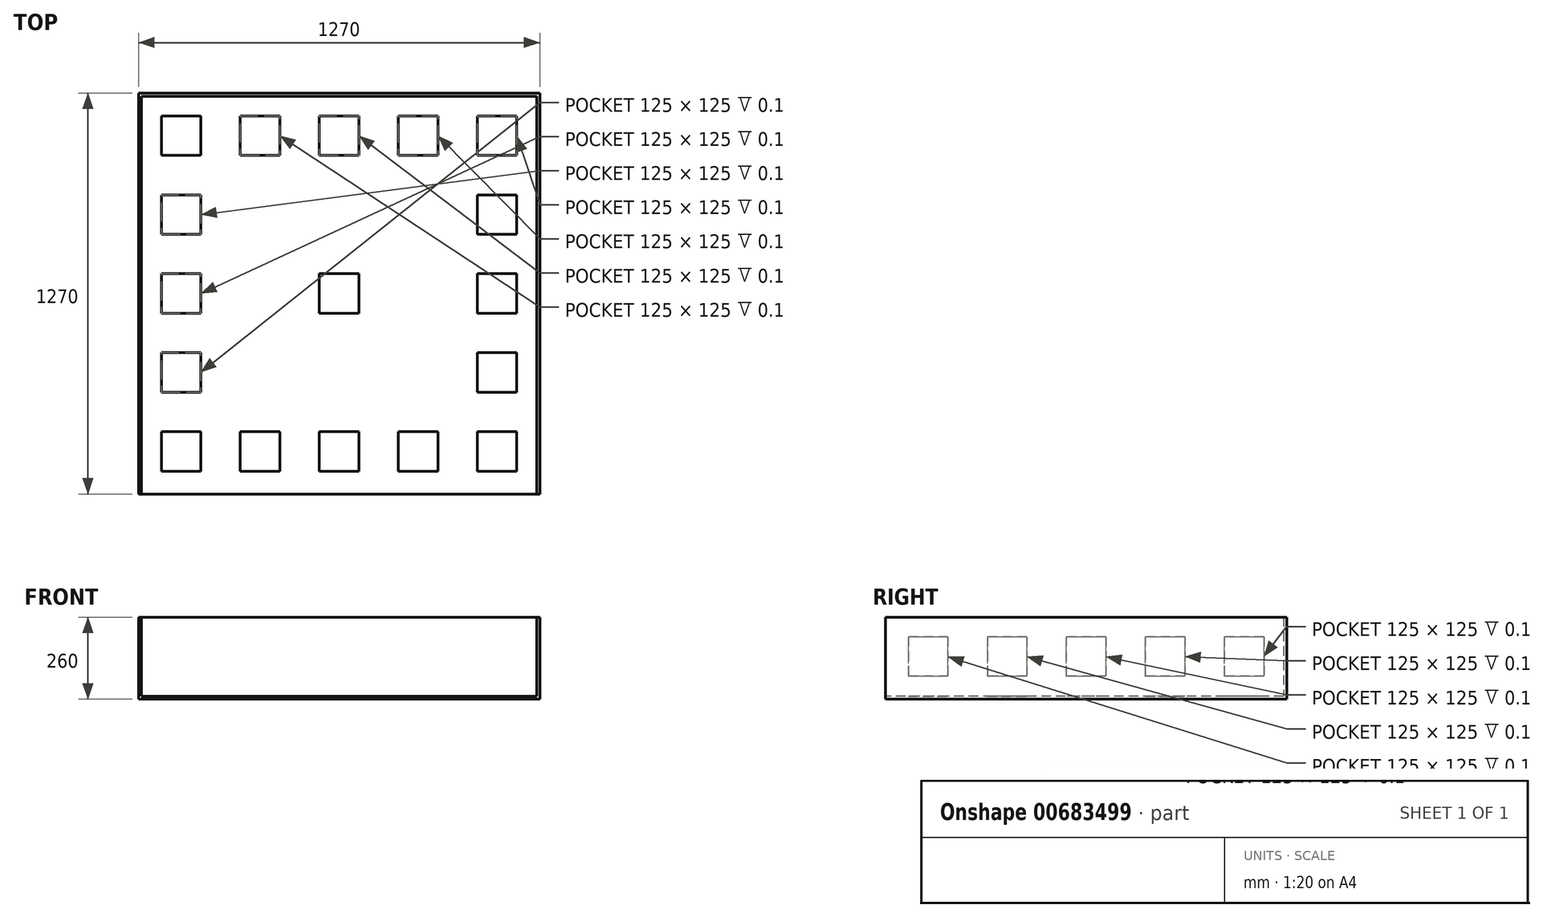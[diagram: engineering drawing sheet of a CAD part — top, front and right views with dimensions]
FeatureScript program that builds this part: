
annotation { "Feature Type Name" : "Feature", "Feature Type Description" : "" }
export const myFeature = defineFeature(function(context is Context, id is Id, definition is map)
    precondition{}
    {
        {
            var Q0;
            Q0=qCreatedBy(makeId("Top.planeOp"),FACE);
            var sketch = newSketch(context, id + "F0", { "sketchPlane" : qUnion([Q0])});
            skLineSegment(sketch, "E0.bottom", {"start": v(500, 500) * mm, "end": v(-500, 500) * mm, "construction": true});
            skLineSegment(sketch, "E0.top", {"start": v(500, -500) * mm, "end": v(-500, -500) * mm, "construction": true});
            skLineSegment(sketch, "E0.left", {"start": v(500, 500) * mm, "end": v(500, -500) * mm, "construction": true});
            skLineSegment(sketch, "E0.right", {"start": v(-500, 500) * mm, "end": v(-500, -500) * mm, "construction": true});
            skPoint(sketch, "E0.middle", {"position": v(0, 0) * mm});
            skLineSegment(sketch, "E1.bottom", {"start": v(-562.5, 562.5) * mm, "end": v(-437.5, 562.5) * mm});
            skLineSegment(sketch, "E1.top", {"start": v(-562.5, 437.5) * mm, "end": v(-437.5, 437.5) * mm});
            skLineSegment(sketch, "E1.left", {"start": v(-562.5, 562.5) * mm, "end": v(-562.5, 437.5) * mm});
            skLineSegment(sketch, "E1.right", {"start": v(-437.5, 562.5) * mm, "end": v(-437.5, 437.5) * mm});
            skPoint(sketch, "E1.middle", {"position": v(-500, 500) * mm});
            skLineSegment(sketch, "E2.1.0.0", {"start": v(-312.5, 562.5) * mm, "end": v(-187.5, 562.5) * mm});
            skLineSegment(sketch, "E2.1.0.1", {"start": v(-187.5, 562.5) * mm, "end": v(-187.5, 437.5) * mm});
            skLineSegment(sketch, "E2.1.0.2", {"start": v(-312.5, 437.5) * mm, "end": v(-187.5, 437.5) * mm});
            skLineSegment(sketch, "E2.1.0.3", {"start": v(-312.5, 562.5) * mm, "end": v(-312.5, 437.5) * mm});
            skLineSegment(sketch, "E2.2.0.0", {"start": v(-62.5, 562.5) * mm, "end": v(62.5, 562.5) * mm});
            skLineSegment(sketch, "E2.2.0.1", {"start": v(62.5, 562.5) * mm, "end": v(62.5, 437.5) * mm});
            skLineSegment(sketch, "E2.2.0.2", {"start": v(-62.5, 437.5) * mm, "end": v(62.5, 437.5) * mm});
            skLineSegment(sketch, "E2.2.0.3", {"start": v(-62.5, 562.5) * mm, "end": v(-62.5, 437.5) * mm});
            skLineSegment(sketch, "E2.3.0.0", {"start": v(187.5, 562.5) * mm, "end": v(312.5, 562.5) * mm});
            skLineSegment(sketch, "E2.3.0.1", {"start": v(312.5, 562.5) * mm, "end": v(312.5, 437.5) * mm});
            skLineSegment(sketch, "E2.3.0.2", {"start": v(187.5, 437.5) * mm, "end": v(312.5, 437.5) * mm});
            skLineSegment(sketch, "E2.3.0.3", {"start": v(187.5, 562.5) * mm, "end": v(187.5, 437.5) * mm});
            skLineSegment(sketch, "E2.4.0.0", {"start": v(437.5, 562.5) * mm, "end": v(562.5, 562.5) * mm});
            skLineSegment(sketch, "E2.4.0.1", {"start": v(562.5, 562.5) * mm, "end": v(562.5, 437.5) * mm});
            skLineSegment(sketch, "E2.4.0.2", {"start": v(437.5, 437.5) * mm, "end": v(562.5, 437.5) * mm});
            skLineSegment(sketch, "E2.4.0.3", {"start": v(437.5, 562.5) * mm, "end": v(437.5, 437.5) * mm});
            skLineSegment(sketch, "E2.direction1", {"start": v(-562.5, 562.5) * mm, "end": v(-312.5, 562.5) * mm, "construction": true});
            skLineSegment(sketch, "E3.0.1.0", {"start": v(-437.5, 312.5) * mm, "end": v(-437.5, 187.5) * mm});
            skLineSegment(sketch, "E3.0.1.1", {"start": v(-562.5, 312.5) * mm, "end": v(-562.5, 187.5) * mm});
            skLineSegment(sketch, "E3.0.1.2", {"start": v(-562.5, 187.5) * mm, "end": v(-437.5, 187.5) * mm});
            skLineSegment(sketch, "E3.0.2.0", {"start": v(-437.5, 62.5) * mm, "end": v(-437.5, -62.5) * mm});
            skLineSegment(sketch, "E3.0.2.1", {"start": v(-562.5, 62.5) * mm, "end": v(-562.5, -62.5) * mm});
            skLineSegment(sketch, "E3.0.2.2", {"start": v(-562.5, -62.5) * mm, "end": v(-437.5, -62.5) * mm});
            skLineSegment(sketch, "E3.0.3.0", {"start": v(-437.5, -187.5) * mm, "end": v(-437.5, -312.5) * mm});
            skLineSegment(sketch, "E3.0.3.1", {"start": v(-562.5, -187.5) * mm, "end": v(-562.5, -312.5) * mm});
            skLineSegment(sketch, "E3.0.3.2", {"start": v(-562.5, -312.5) * mm, "end": v(-437.5, -312.5) * mm});
            skLineSegment(sketch, "E3.0.4.0", {"start": v(-437.5, -437.5) * mm, "end": v(-437.5, -562.5) * mm});
            skLineSegment(sketch, "E3.0.4.1", {"start": v(-562.5, -437.5) * mm, "end": v(-562.5, -562.5) * mm});
            skLineSegment(sketch, "E3.0.4.2", {"start": v(-562.5, -562.5) * mm, "end": v(-437.5, -562.5) * mm});
            skLineSegment(sketch, "E3.direction1", {"start": v(-437.5, 437.5) * mm, "end": v(-412.1, 437.5) * mm, "construction": true});
            skLineSegment(sketch, "E3.direction2", {"start": v(-437.5, 437.5) * mm, "end": v(-437.5, 187.5) * mm, "construction": true});
            skLineSegment(sketch, "E4", {"start": v(-562.5, 312.5) * mm, "end": v(-437.5, 312.5) * mm});
            skLineSegment(sketch, "E5", {"start": v(-562.5, 62.5) * mm, "end": v(-437.5, 62.5) * mm});
            skLineSegment(sketch, "E6", {"start": v(-562.5, -187.5) * mm, "end": v(-437.5, -187.5) * mm});
            skLineSegment(sketch, "E7", {"start": v(-562.5, -437.5) * mm, "end": v(-437.5, -437.5) * mm});
            skLineSegment(sketch, "E8", {"start": v(500, 500) * mm, "end": v(-500, -500) * mm, "construction": true});
            skLineSegment(sketch, "E9.MirrorCS", {"start": v(437.5, -437.5) * mm, "end": v(437.5, -412.1) * mm, "construction": true});
            skLineSegment(sketch, "E10.MirrorCS", {"start": v(312.5, -437.5) * mm, "end": v(187.5, -437.5) * mm});
            skLineSegment(sketch, "E11.MirrorCS", {"start": v(562.5, -562.5) * mm, "end": v(562.5, -437.5) * mm});
            skPoint(sketch, "E12.MirrorP", {"position": v(500, -500) * mm});
            skLineSegment(sketch, "E13.MirrorCS", {"start": v(437.5, 187.5) * mm, "end": v(437.5, 312.5) * mm});
            skLineSegment(sketch, "E14.MirrorCS", {"start": v(312.5, -562.5) * mm, "end": v(187.5, -562.5) * mm});
            skLineSegment(sketch, "E15.MirrorCS", {"start": v(-187.5, -437.5) * mm, "end": v(-312.5, -437.5) * mm});
            skLineSegment(sketch, "E16.MirrorCS", {"start": v(562.5, -562.5) * mm, "end": v(562.5, -312.5) * mm, "construction": true});
            skLineSegment(sketch, "E17.MirrorCS", {"start": v(437.5, -437.5) * mm, "end": v(187.5, -437.5) * mm, "construction": true});
            skLineSegment(sketch, "E18.MirrorCS", {"start": v(562.5, 187.5) * mm, "end": v(437.5, 187.5) * mm});
            skLineSegment(sketch, "E19.MirrorCS", {"start": v(562.5, 62.5) * mm, "end": v(437.5, 62.5) * mm});
            skLineSegment(sketch, "E20.MirrorCS", {"start": v(437.5, -62.5) * mm, "end": v(437.5, 62.5) * mm});
            skLineSegment(sketch, "E21.MirrorCS", {"start": v(562.5, -62.5) * mm, "end": v(437.5, -62.5) * mm});
            skLineSegment(sketch, "E22.MirrorCS", {"start": v(437.5, -562.5) * mm, "end": v(437.5, -437.5) * mm});
            skLineSegment(sketch, "E23.MirrorCS", {"start": v(562.5, -562.5) * mm, "end": v(437.5, -562.5) * mm});
            skLineSegment(sketch, "E24.MirrorCS", {"start": v(562.5, 187.5) * mm, "end": v(562.5, 312.5) * mm});
            skLineSegment(sketch, "E25.MirrorCS", {"start": v(62.5, -562.5) * mm, "end": v(-62.5, -562.5) * mm});
            skLineSegment(sketch, "E26.MirrorCS", {"start": v(-187.5, -562.5) * mm, "end": v(-187.5, -437.5) * mm});
            skLineSegment(sketch, "E27.MirrorCS", {"start": v(312.5, -562.5) * mm, "end": v(312.5, -437.5) * mm});
            skLineSegment(sketch, "E28.MirrorCS", {"start": v(187.5, -562.5) * mm, "end": v(187.5, -437.5) * mm});
            skLineSegment(sketch, "E29.MirrorCS", {"start": v(562.5, -312.5) * mm, "end": v(437.5, -312.5) * mm});
            skLineSegment(sketch, "E30.MirrorCS", {"start": v(437.5, -312.5) * mm, "end": v(437.5, -187.5) * mm});
            skLineSegment(sketch, "E31.MirrorCS", {"start": v(562.5, -187.5) * mm, "end": v(437.5, -187.5) * mm});
            skLineSegment(sketch, "E32.MirrorCS", {"start": v(-312.5, -562.5) * mm, "end": v(-312.5, -437.5) * mm});
            skLineSegment(sketch, "E33.MirrorCS", {"start": v(562.5, 312.5) * mm, "end": v(437.5, 312.5) * mm});
            skLineSegment(sketch, "E34.MirrorCS", {"start": v(562.5, -312.5) * mm, "end": v(562.5, -187.5) * mm});
            skLineSegment(sketch, "E35.MirrorCS", {"start": v(62.5, -437.5) * mm, "end": v(-62.5, -437.5) * mm});
            skLineSegment(sketch, "E36.MirrorCS", {"start": v(62.5, -562.5) * mm, "end": v(62.5, -437.5) * mm});
            skLineSegment(sketch, "E37.MirrorCS", {"start": v(562.5, -437.5) * mm, "end": v(437.5, -437.5) * mm});
            skLineSegment(sketch, "E38.MirrorCS", {"start": v(-62.5, -562.5) * mm, "end": v(-62.5, -437.5) * mm});
            skLineSegment(sketch, "E39.MirrorCS", {"start": v(562.5, -62.5) * mm, "end": v(562.5, 62.5) * mm});
            skLineSegment(sketch, "E40.MirrorCS", {"start": v(-187.5, -562.5) * mm, "end": v(-312.5, -562.5) * mm});
            skLineSegment(sketch, "E41.bottom", {"start": v(-62.5, 62.5) * mm, "end": v(62.5, 62.5) * mm});
            skLineSegment(sketch, "E41.top", {"start": v(-62.5, -62.5) * mm, "end": v(62.5, -62.5) * mm});
            skLineSegment(sketch, "E41.left", {"start": v(-62.5, 62.5) * mm, "end": v(-62.5, -62.5) * mm});
            skLineSegment(sketch, "E41.right", {"start": v(62.5, 62.5) * mm, "end": v(62.5, -62.5) * mm});
            skSolve(sketch);
        }
        {
            var Q0;
            Q0=qCreatedBy(makeId("Top.planeOp"),FACE);
            var sketch = newSketch(context, id + "F1", { "sketchPlane" : qUnion([Q0])});
            skLineSegment(sketch, "E42.bottom", {"start": v(-625, 625) * mm, "end": v(625, 625) * mm});
            skLineSegment(sketch, "E42.top", {"start": v(-625, -625) * mm, "end": v(625, -625) * mm});
            skLineSegment(sketch, "E42.left", {"start": v(-625, 625) * mm, "end": v(-625, -625) * mm});
            skLineSegment(sketch, "E42.right", {"start": v(625, 625) * mm, "end": v(625, -625) * mm});
            skPoint(sketch, "E42.middle", {"position": v(0, 0) * mm});
            skSolve(sketch);
        }
        {
            var Q0;
            Q0 = qSketchRegion(id + "F1", true);
            extrude(context, id + "F2", {"entities" : qUnion([Q0]), "oppositeDirection" : true, "depth" : 10 * mm, "offsetDistance" : 25.4 * mm});
        }
        {
            var Q0;
            Q0 = qSketchRegion(id + "F0", true);
            extrude(context, id + "F3", {"entities" : qUnion([Q0]), "operationType" : NewBodyOperationType.REMOVE, "oppositeDirection" : true, "depth" : 0.1 * mm, "offsetDistance" : 25.4 * mm});
        }
        {
            var Q0;
            Q0=makeQuery(id+"F2.opExtrude","CAP_FACE",FACE,{"disambiguationData":[OSD([sQuery(id+"F1.wireOp",EDGE,"E42.bottom"),sQuery(id+"F1.wireOp",EDGE,"E42.top"),sQuery(id+"F1.wireOp",EDGE,"E42.left"),sQuery(id+"F1.wireOp",EDGE,"E42.right")])],"isStart":false});
            var sketch = newSketch(context, id + "F4", { "sketchPlane" : qUnion([Q0])});
            skLineSegment(sketch, "E43.bottom", {"start": v(635, 635) * mm, "end": v(-635, 635) * mm});
            skLineSegment(sketch, "E43.top", {"start": v(635, -635) * mm, "end": v(-635, -635) * mm});
            skLineSegment(sketch, "E43.left", {"start": v(635, 635) * mm, "end": v(635, -635) * mm});
            skLineSegment(sketch, "E43.right", {"start": v(-635, 635) * mm, "end": v(-635, -635) * mm});
            skPoint(sketch, "E43.middle", {"position": v(0, 0) * mm});
            skLineSegment(sketch, "E44.bottom", {"start": v(-625, 625) * mm, "end": v(625, 625) * mm});
            skLineSegment(sketch, "E44.top", {"start": v(-625, -625) * mm, "end": v(625, -625) * mm});
            skLineSegment(sketch, "E44.left", {"start": v(-625, 625) * mm, "end": v(-625, -625) * mm});
            skLineSegment(sketch, "E44.right", {"start": v(625, 625) * mm, "end": v(625, -625) * mm});
            skSolve(sketch);
        }
        {
            var Q0;
            Q0 = qSketchRegion(id + "F4", true);
            extrude(context, id + "F5", {"entities" : qUnion([Q0]), "operationType" : NewBodyOperationType.ADD, "oppositeDirection" : true, "depth" : 260 * mm, "offsetDistance" : 25.4 * mm});
        }
        {
            var Q0;
            Q0=makeQuery(id+"F5.opExtrude","SWEPT_FACE",FACE,{"disambiguationData":[OSD([sQuery(id+"F4.wireOp",EDGE,"E44.left")])]});
            var sketch = newSketch(context, id + "F6", { "sketchPlane" : qUnion([Q0])});
            skLineSegment(sketch, "E45.bottom", {"start": v(-437.5, 187.5) * mm, "end": v(-562.5, 187.5) * mm});
            skLineSegment(sketch, "E45.top", {"start": v(-437.5, 62.5) * mm, "end": v(-562.5, 62.5) * mm});
            skLineSegment(sketch, "E45.left", {"start": v(-437.5, 187.5) * mm, "end": v(-437.5, 62.5) * mm});
            skLineSegment(sketch, "E45.right", {"start": v(-562.5, 187.5) * mm, "end": v(-562.5, 62.5) * mm});
            skPoint(sketch, "E45.middle", {"position": v(-500, 125) * mm});
            skLineSegment(sketch, "E46.1.0.0", {"start": v(-187.5, 62.5) * mm, "end": v(-312.5, 62.5) * mm});
            skLineSegment(sketch, "E46.1.0.1", {"start": v(-187.5, 187.5) * mm, "end": v(-187.5, 62.5) * mm});
            skLineSegment(sketch, "E46.1.0.2", {"start": v(-312.5, 187.5) * mm, "end": v(-312.5, 62.5) * mm});
            skLineSegment(sketch, "E46.1.0.3", {"start": v(-187.5, 187.5) * mm, "end": v(-312.5, 187.5) * mm});
            skPoint(sketch, "E46.1.0.4", {"position": v(-250, 125) * mm});
            skLineSegment(sketch, "E46.2.0.0", {"start": v(62.5, 62.5) * mm, "end": v(-62.5, 62.5) * mm});
            skLineSegment(sketch, "E46.2.0.1", {"start": v(62.5, 187.5) * mm, "end": v(62.5, 62.5) * mm});
            skLineSegment(sketch, "E46.2.0.2", {"start": v(-62.5, 187.5) * mm, "end": v(-62.5, 62.5) * mm});
            skLineSegment(sketch, "E46.2.0.3", {"start": v(62.5, 187.5) * mm, "end": v(-62.5, 187.5) * mm});
            skPoint(sketch, "E46.2.0.4", {"position": v(0, 125) * mm});
            skLineSegment(sketch, "E46.3.0.0", {"start": v(312.5, 62.5) * mm, "end": v(187.5, 62.5) * mm});
            skLineSegment(sketch, "E46.3.0.1", {"start": v(312.5, 187.5) * mm, "end": v(312.5, 62.5) * mm});
            skLineSegment(sketch, "E46.3.0.2", {"start": v(187.5, 187.5) * mm, "end": v(187.5, 62.5) * mm});
            skLineSegment(sketch, "E46.3.0.3", {"start": v(312.5, 187.5) * mm, "end": v(187.5, 187.5) * mm});
            skPoint(sketch, "E46.3.0.4", {"position": v(250, 125) * mm});
            skLineSegment(sketch, "E46.4.0.0", {"start": v(562.5, 62.5) * mm, "end": v(437.5, 62.5) * mm});
            skLineSegment(sketch, "E46.4.0.1", {"start": v(562.5, 187.5) * mm, "end": v(562.5, 62.5) * mm});
            skLineSegment(sketch, "E46.4.0.2", {"start": v(437.5, 187.5) * mm, "end": v(437.5, 62.5) * mm});
            skLineSegment(sketch, "E46.4.0.3", {"start": v(562.5, 187.5) * mm, "end": v(437.5, 187.5) * mm});
            skPoint(sketch, "E46.4.0.4", {"position": v(500, 125) * mm});
            skLineSegment(sketch, "E46.direction1", {"start": v(-562.5, 62.5) * mm, "end": v(-312.5, 62.5) * mm, "construction": true});
            skSolve(sketch);
        }
        {
            var Q0;
            Q0 = qSketchRegion(id + "F6", true);
            extrude(context, id + "F7", {"entities" : qUnion([Q0]), "operationType" : NewBodyOperationType.REMOVE, "oppositeDirection" : true, "depth" : 0.1 * mm, "offsetDistance" : 25.4 * mm});
        }
        {
            var Q0;
            Q0=qCreatedBy(makeId("Front.planeOp"),FACE);
            var sketch = newSketch(context, id + "F8", { "sketchPlane" : qUnion([Q0])});
            skLineSegment(sketch, "E47", {"start": v(0, 0) * mm, "end": v(0, 412.57) * mm});
            skSolve(sketch);
        }
        {
            var Q0;
            Q0=makeQuery(id+"F5.opExtrude","CAP_FACE",FACE,{"disambiguationData":[OSD([sQuery(id+"F4.wireOp",EDGE,"E43.bottom"),sQuery(id+"F4.wireOp",EDGE,"E43.top"),sQuery(id+"F4.wireOp",EDGE,"E43.left"),sQuery(id+"F4.wireOp",EDGE,"E43.right"),sQuery(id+"F4.wireOp",EDGE,"E44.bottom"),sQuery(id+"F4.wireOp",EDGE,"E44.top"),sQuery(id+"F4.wireOp",EDGE,"E44.left"),sQuery(id+"F4.wireOp",EDGE,"E44.right")])],"isStart":false});
            var sketch = newSketch(context, id + "F9", { "sketchPlane" : qUnion([Q0])});
            skLineSegment(sketch, "E48.bottom", {"start": v(-625, -625) * mm, "end": v(625, -625) * mm});
            skLineSegment(sketch, "E48.top", {"start": v(-625, -635) * mm, "end": v(625, -635) * mm});
            skLineSegment(sketch, "E48.left", {"start": v(-625, -625) * mm, "end": v(-625, -635) * mm});
            skLineSegment(sketch, "E48.right", {"start": v(625, -625) * mm, "end": v(625, -635) * mm});
            skSolve(sketch);
        }
        {
            var Q0;
            Q0=makeQuery(id+"F9.imprint","IMPRINT",FACE,{"disambiguationData":[TD([[makeQuery(id+"F9.imprint","IMPRINT",EDGE,{"derivedFrom":sQuery(id+"F9.wireOp",EDGE,"E48.bottom")}),-1.0]])]});
            var Q1;
            Q1=makeQuery(id+"F2.opExtrude","CAP_FACE",FACE,{"disambiguationData":[OSD([sQuery(id+"F1.wireOp",EDGE,"E42.bottom"),sQuery(id+"F1.wireOp",EDGE,"E42.top"),sQuery(id+"F1.wireOp",EDGE,"E42.left"),sQuery(id+"F1.wireOp",EDGE,"E42.right")])],"isStart":true});
            extrude(context, id + "F10", {"entities" : qUnion([Q0]), "operationType" : NewBodyOperationType.REMOVE, "endBound" : BoundingType.UP_TO_SURFACE, "oppositeDirection" : true, "depth" : 25.4 * mm, "endBoundEntityFace" : qUnion([Q1]), "offsetDistance" : 25.4 * mm});
        }
    });
